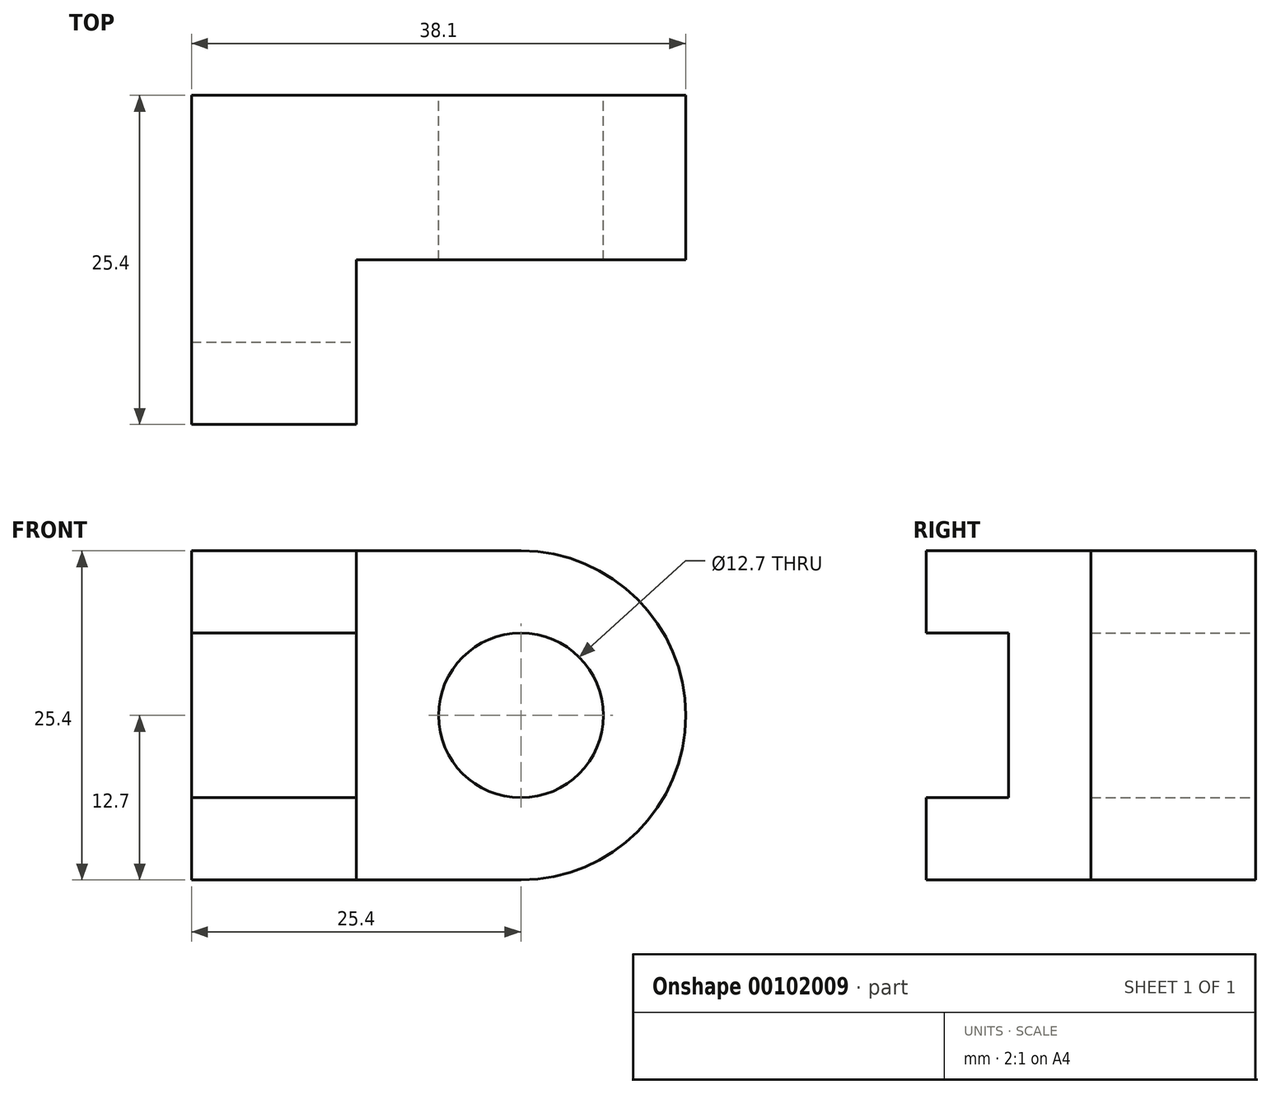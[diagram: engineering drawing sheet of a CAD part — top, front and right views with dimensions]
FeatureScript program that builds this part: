
annotation { "Feature Type Name" : "Feature", "Feature Type Description" : "" }
export const myFeature = defineFeature(function(context is Context, id is Id, definition is map)
    precondition{}
    {
        {
            var Q0;
            Q0=qCreatedBy(makeId("Front.planeOp"),FACE);
            var sketch = newSketch(context, id + "F0", { "sketchPlane" : qUnion([Q0])});
            skLineSegment(sketch, "E0.bottom", {"start": v(0, 0) * mm, "end": v(25.4, 0) * mm});
            skLineSegment(sketch, "E0.top", {"start": v(0, 25.4) * mm, "end": v(25.4, 25.4) * mm});
            skLineSegment(sketch, "E0.left", {"start": v(0, 0) * mm, "end": v(0, 25.4) * mm});
            skLineSegment(sketch, "E0.right", {"start": v(25.4, 0) * mm, "end": v(25.4, 25.4) * mm, "construction": true});
            skCircle(sketch, "E1", {"center": v(25.4, 12.7) * mm, "radius": 6.35 * mm});
            skArc(sketch, "E2", {"start": v(25.4, 0) * mm, "mid": v(38.1, 12.7) * mm, "end": v(25.4, 25.4) * mm});
            skSolve(sketch);
        }
        {
            var Q0;
            Q0 = qSketchRegion(id + "F0", true);
            extrude(context, id + "F1", {"entities" : qUnion([Q0]), "endBound" : BoundingType.SYMMETRIC, "depth" : 12.7 * mm});
        }
        {
            var Q0;
            Q0=qCreatedBy(makeId("Front.planeOp"),FACE);
            var sketch = newSketch(context, id + "F2", { "sketchPlane" : qUnion([Q0])});
            skLineSegment(sketch, "E3", {"start": v(0, 0) * mm, "end": v(0, 25.4) * mm});
            skLineSegment(sketch, "E4", {"start": v(0, 25.4) * mm, "end": v(12.7, 25.4) * mm});
            skLineSegment(sketch, "E5", {"start": v(12.7, 25.4) * mm, "end": v(12.7, 0) * mm});
            skLineSegment(sketch, "E6", {"start": v(12.7, 0) * mm, "end": v(0, 0) * mm});
            skSolve(sketch);
        }
        {
            var Q0;
            Q0 = qSketchRegion(id + "F2", true);
            extrude(context, id + "F3", {"entities" : qUnion([Q0]), "operationType" : NewBodyOperationType.ADD, "depth" : 12.7 * mm});
        }
        {
            var Q0;
            Q0=qCreatedBy(makeId("Front.planeOp"),FACE);
            var sketch = newSketch(context, id + "F4", { "sketchPlane" : qUnion([Q0])});
            skLineSegment(sketch, "E7", {"start": v(0, 0) * mm, "end": v(0, 6.35) * mm});
            skLineSegment(sketch, "E8", {"start": v(0, 6.35) * mm, "end": v(12.7, 6.35) * mm});
            skLineSegment(sketch, "E9", {"start": v(12.7, 6.35) * mm, "end": v(12.7, 0) * mm});
            skLineSegment(sketch, "E10", {"start": v(12.7, 0) * mm, "end": v(0, 0) * mm});
            skLineSegment(sketch, "E11", {"start": v(0, 6.35) * mm, "end": v(0, 19.05) * mm, "construction": true});
            skLineSegment(sketch, "E12", {"start": v(0, 19.05) * mm, "end": v(0, 25.4) * mm});
            skLineSegment(sketch, "E13", {"start": v(0, 25.4) * mm, "end": v(12.7, 25.4) * mm});
            skLineSegment(sketch, "E14", {"start": v(12.7, 25.4) * mm, "end": v(12.7, 19.05) * mm});
            skLineSegment(sketch, "E15", {"start": v(12.7, 19.05) * mm, "end": v(0, 19.05) * mm});
            skSolve(sketch);
        }
        {
            var Q0;
            Q0 = qSketchRegion(id + "F4", true);
            extrude(context, id + "F5", {"entities" : qUnion([Q0]), "operationType" : NewBodyOperationType.ADD, "depth" : 19.05 * mm});
        }
    });
